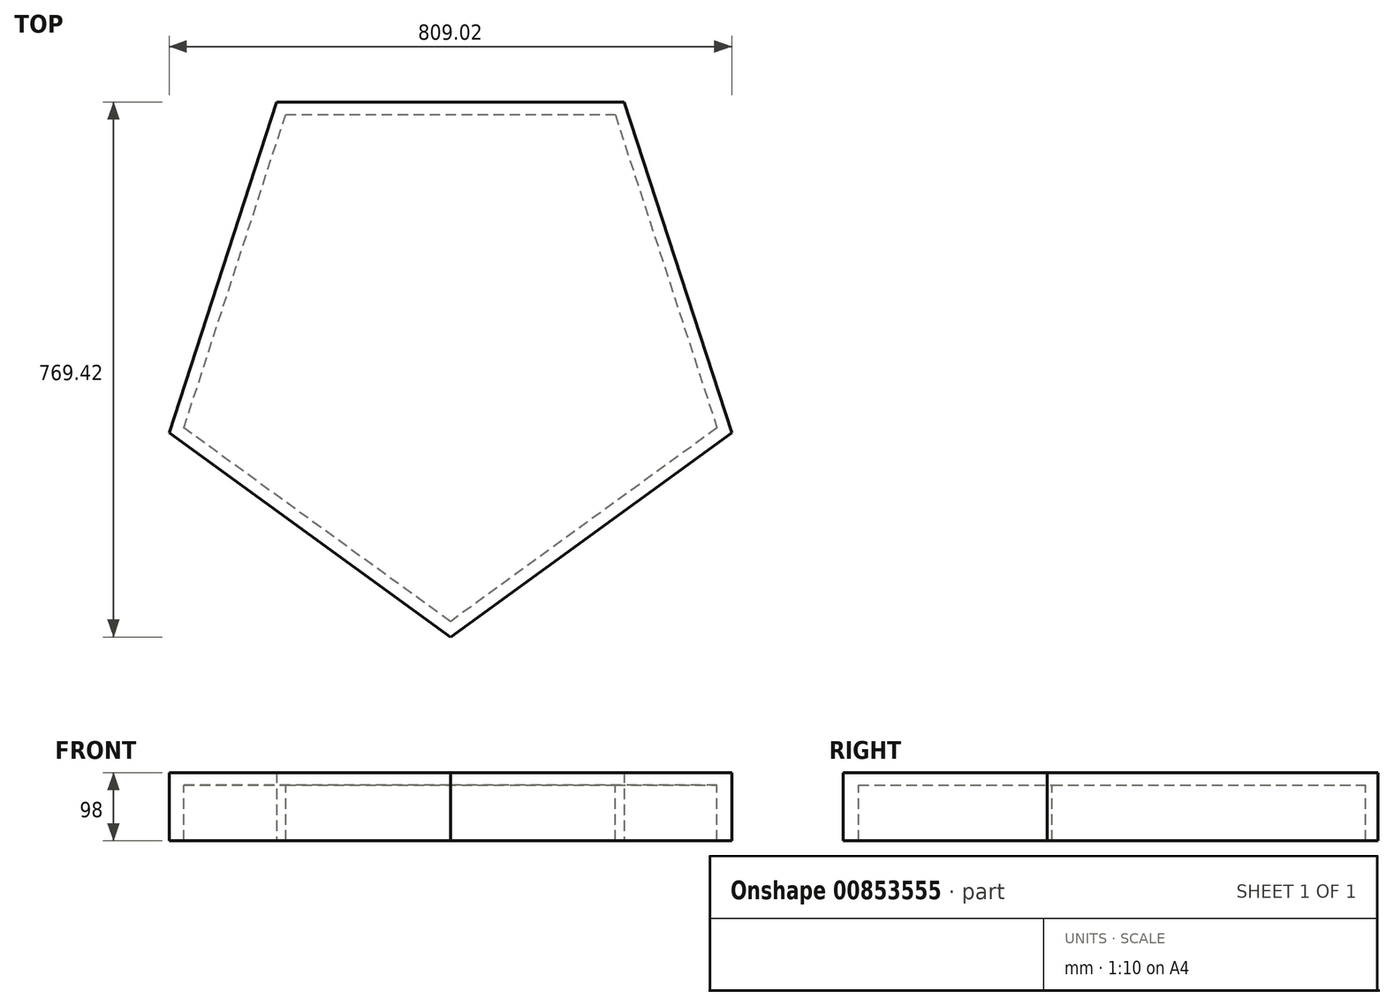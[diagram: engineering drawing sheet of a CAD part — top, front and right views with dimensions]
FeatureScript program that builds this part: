
annotation { "Feature Type Name" : "Feature", "Feature Type Description" : "" }
export const myFeature = defineFeature(function(context is Context, id is Id, definition is map)
    precondition{}
    {
        {
            var Q0;
            Q0=qCreatedBy(makeId("Top.planeOp"),FACE);
            var sketch = newSketch(context, id + "F0", { "sketchPlane" : qUnion([Q0])});
            skLineSegment(sketch, "E0", {"start": v(289.88, 358.02) * mm, "end": v(-210.12, 358.02) * mm});
            skLineSegment(sketch, "E1", {"start": v(-210.12, 358.02) * mm, "end": v(-364.63, -117.5) * mm});
            skLineSegment(sketch, "E2", {"start": v(-364.63, -117.5) * mm, "end": v(39.88, -411.4) * mm});
            skLineSegment(sketch, "E3", {"start": v(39.88, -411.4) * mm, "end": v(444.39, -117.5) * mm});
            skLineSegment(sketch, "E4", {"start": v(289.88, 358.02) * mm, "end": v(444.39, -117.5) * mm});
            skSolve(sketch);
        }
        {
            var Q0;
            Q0=makeQuery(id+"F0.imprint","IMPRINT",FACE,{"disambiguationData":[TD([[makeQuery(id+"F0.imprint","IMPRINT",EDGE,{"derivedFrom":sQuery(id+"F0.wireOp",EDGE,"E0")}),1.0]])]});
            extrude(context, id + "F1", {"entities" : qUnion([Q0]), "depth" : 18 * mm, "offsetDistance" : 25 * mm});
        }
        {
            var Q0;
            Q0=makeQuery(id+"F1.opExtrude","CAP_FACE",FACE,{"disambiguationData":[OSD([sQuery(id+"F0.wireOp",EDGE,"E0"),sQuery(id+"F0.wireOp",EDGE,"E1"),sQuery(id+"F0.wireOp",EDGE,"E2"),sQuery(id+"F0.wireOp",EDGE,"E3"),sQuery(id+"F0.wireOp",EDGE,"E4")])],"isStart":true});
            var sketch = newSketch(context, id + "F2", { "sketchPlane" : qUnion([Q0])});
            skLineSegment(sketch, "E5", {"start": v(-210.12, -358.02) * mm, "end": v(289.88, -358.02) * mm});
            skLineSegment(sketch, "E6", {"start": v(289.88, -358.02) * mm, "end": v(444.39, 117.5) * mm});
            skLineSegment(sketch, "E7", {"start": v(444.39, 117.5) * mm, "end": v(39.88, 411.4) * mm});
            skLineSegment(sketch, "E8", {"start": v(39.88, 411.4) * mm, "end": v(-364.63, 117.5) * mm});
            skLineSegment(sketch, "E9", {"start": v(-364.63, 117.5) * mm, "end": v(-210.12, -358.02) * mm});
            skLineSegment(sketch, "E10", {"start": v(-197.04, -340.02) * mm, "end": v(276.8, -340.02) * mm});
            skLineSegment(sketch, "E11", {"start": v(276.8, -340.02) * mm, "end": v(423.23, 110.63) * mm});
            skLineSegment(sketch, "E12", {"start": v(423.23, 110.63) * mm, "end": v(39.88, 389.15) * mm});
            skLineSegment(sketch, "E13", {"start": v(39.88, 389.15) * mm, "end": v(-343.47, 110.63) * mm});
            skLineSegment(sketch, "E14", {"start": v(-343.47, 110.63) * mm, "end": v(-197.04, -340.02) * mm});
            skSolve(sketch);
        }
        {
            var Q0;
            Q0=makeQuery(id+"F2.imprint","IMPRINT",FACE,{"disambiguationData":[TD([[makeQuery(id+"F2.imprint","IMPRINT",EDGE,{"derivedFrom":sQuery(id+"F2.wireOp",EDGE,"E5")}),-1.0]])]});
            extrude(context, id + "F3", {"entities" : qUnion([Q0]), "operationType" : NewBodyOperationType.ADD, "depth" : 80 * mm, "offsetDistance" : 25 * mm});
        }
    });
